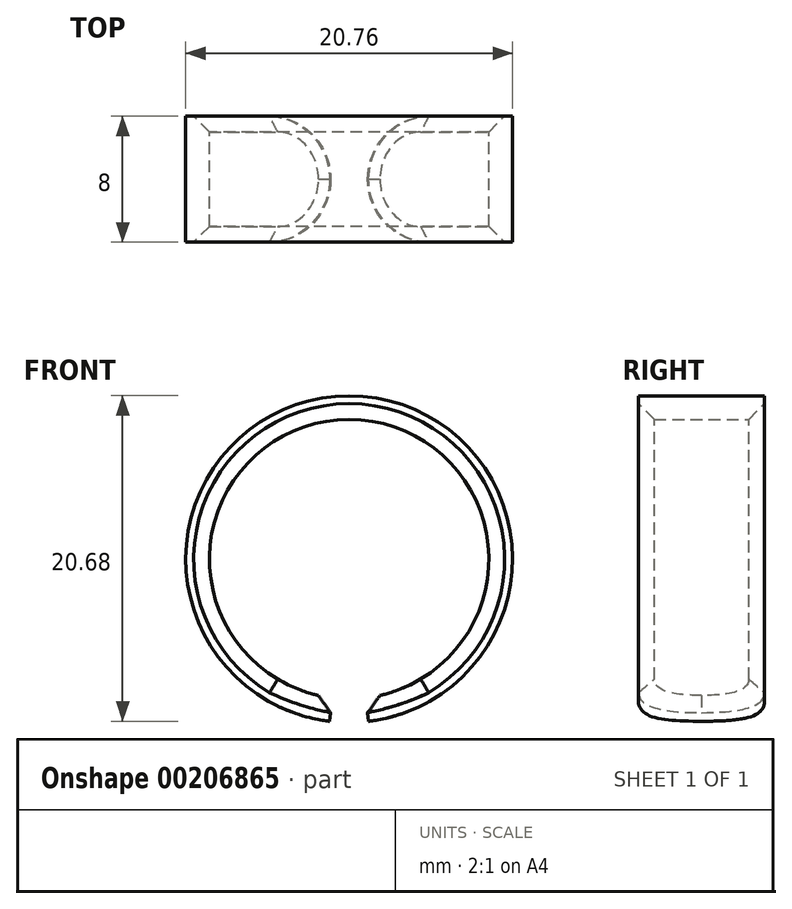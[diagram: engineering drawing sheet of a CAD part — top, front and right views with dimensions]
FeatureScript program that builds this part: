
annotation { "Feature Type Name" : "Feature", "Feature Type Description" : "" }
export const myFeature = defineFeature(function(context is Context, id is Id, definition is map)
    precondition{}
    {
        {
            var Q0;
            Q0=qCreatedBy(makeId("Front.planeOp"),FACE);
            var sketch = newSketch(context, id + "F0", { "sketchPlane" : qUnion([Q0])});
            skCircle(sketch, "E0", {"center": v(0, 0) * mm, "radius": 8.88 * mm});
            skCircle(sketch, "E1.0", {"center": v(0, 0) * mm, "radius": 10.38 * mm});
            skLineSegment(sketch, "E2", {"start": v(0, 0) * mm, "end": v(-1.24, -10.3) * mm});
            skLineSegment(sketch, "E3.MirrorCS", {"start": v(0, 0) * mm, "end": v(1.24, -10.3) * mm});
            skSolve(sketch);
        }
        {
            var Q0;
            {var subQ0=sQuery(id+"F0.wireOp",EDGE,"E2");var subQ1=sQuery(id+"F0.wireOp",EDGE,"E0");var subQ2=makeQuery(id+"F0.imprint","INTERSECT",VERTEX,{"derivedFrom":[subQ1,subQ0]});Q0=makeQuery(id+"F0.imprint","IMPRINT",FACE,{"disambiguationData":[TD([[makeQuery(id+"F0.imprint","IMPRINT",EDGE,{"disambiguationData":[TD([[subQ2,1.0]])],"derivedFrom":subQ1}),-1.0]])]});}
            extrude(context, id + "F1", {"entities" : qUnion([Q0]), "depth" : 4 * mm, "hasSecondDirection" : true, "secondDirectionOppositeDirection" : true, "secondDirectionDepth" : 4 * mm});
        }
        {
            var Q0;
            Q0=makeQuery(id+"F1.opExtrude","CAP_EDGE",EDGE,{"disambiguationData":[OSD([sQuery(id+"F0.wireOp",EDGE,"E3.MirrorCS")])],"isStart":false});
            var Q1;
            Q1=makeQuery(id+"F1.opExtrude","CAP_EDGE",EDGE,{"disambiguationData":[OSD([sQuery(id+"F0.wireOp",EDGE,"E2")])],"isStart":false});
            var Q2;
            Q2=makeQuery(id+"F1.opExtrude","CAP_EDGE",EDGE,{"disambiguationData":[OSD([sQuery(id+"F0.wireOp",EDGE,"E2")])],"isStart":true});
            var Q3;
            Q3=makeQuery(id+"F1.opExtrude","CAP_EDGE",EDGE,{"disambiguationData":[OSD([sQuery(id+"F0.wireOp",EDGE,"E3.MirrorCS")])],"isStart":true});
            fillet(context, id + "F2", {"entities" : qUnion([Q0, Q1, Q2, Q3]), "radius" : 4 * mm, "tangentPropagation" : true, "allowEdgeOverflow" : false});
        }
        {
            var Q0;
            Q0=makeQuery(id+"F1.opExtrude","CAP_EDGE",EDGE,{"disambiguationData":[OSD([sQuery(id+"F0.wireOp",EDGE,"E0")])],"isStart":true});
            var Q1;
            Q1=makeQuery(id+"F1.opExtrude","CAP_EDGE",EDGE,{"disambiguationData":[OSD([sQuery(id+"F0.wireOp",EDGE,"E0")])],"isStart":false});
            var Q2;
            Q2=makeQuery(id+"F2.opFillet","BLEND_EDGE",EDGE,{"blendedFrom":[makeQuery(id+"F1.opExtrude","CAP_EDGE",EDGE,{"disambiguationData":[OSD([sQuery(id+"F0.wireOp",EDGE,"E2")])],"isStart":false}),makeQuery(id+"F1.opExtrude","SWEPT_FACE",FACE,{"disambiguationData":[OSD([sQuery(id+"F0.wireOp",EDGE,"E0")])]})],"blendedInto":[makeQuery(id+"F1.opExtrude","SWEPT_FACE",FACE,{"disambiguationData":[OSD([sQuery(id+"F0.wireOp",EDGE,"E0")])]})]});
            var Q3;
            Q3=makeQuery(id+"F2.opFillet","BLEND_EDGE",EDGE,{"blendedFrom":[makeQuery(id+"F1.opExtrude","CAP_EDGE",EDGE,{"disambiguationData":[OSD([sQuery(id+"F0.wireOp",EDGE,"E3.MirrorCS")])],"isStart":true}),makeQuery(id+"F1.opExtrude","SWEPT_FACE",FACE,{"disambiguationData":[OSD([sQuery(id+"F0.wireOp",EDGE,"E0")])]})],"blendedInto":[makeQuery(id+"F1.opExtrude","SWEPT_FACE",FACE,{"disambiguationData":[OSD([sQuery(id+"F0.wireOp",EDGE,"E0")])]})]});
            chamfer(context, id + "F3", {"entities" : qUnion([Q0, Q1, Q2, Q3]), "width" : 1 * mm, "tangentPropagation" : true});
        }
    });
